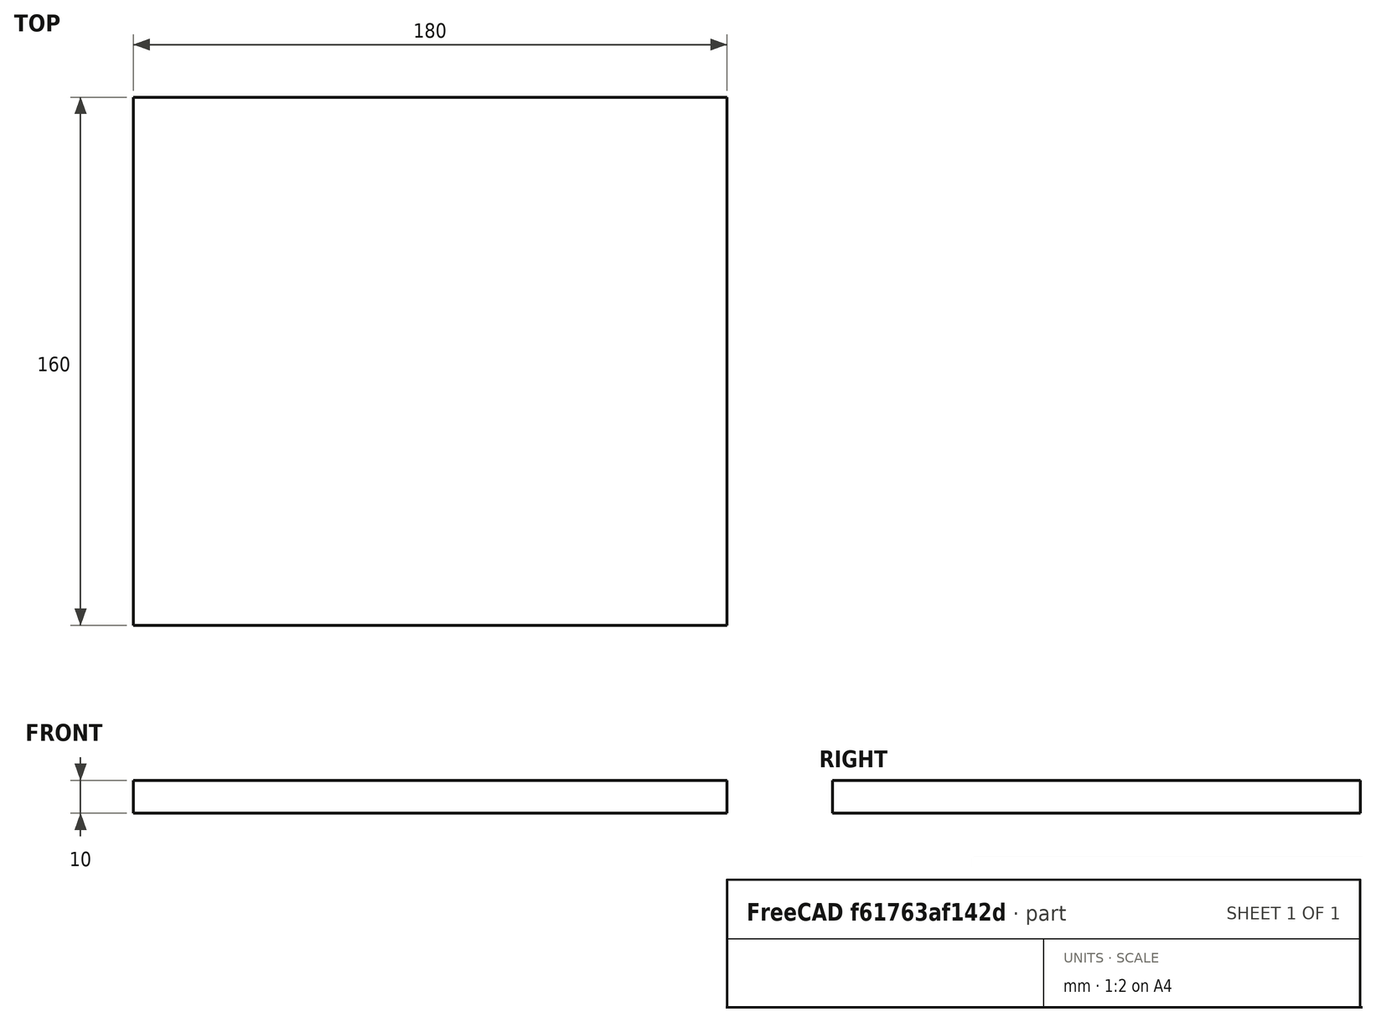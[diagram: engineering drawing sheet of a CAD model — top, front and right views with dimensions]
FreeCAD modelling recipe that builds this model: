
FCSTD DOCUMENT  (FreeCAD 0.18R4 (GitTag))
Label: BottomBaseMedium
License: All rights reserved
LicenseURL: http://en.wikipedia.org/wiki/All_rights_reserved
objects: Sketcher::SketchObject×1, PartDesign::Pad×1, PartDesign::Body×1
note: 4 computed .brp shape members not serialized (recipe doc carries the construction recipe); baked Part::Feature solids carry a one-line shape summary decoded from their .brp

FEATURE [Sketcher::SketchObject] Sketch
  MapMode = 5
  Support = -> [XY_Plane]
  sketch-geometry (4):
    g0: LineSegment StartX=0 StartY=0 StartZ=0 EndX=-180 EndY=0 EndZ=0
    g1: LineSegment StartX=-180 StartY=0 StartZ=0 EndX=-180 EndY=160 EndZ=0
    g2: LineSegment StartX=-180 StartY=160 StartZ=0 EndX=0 EndY=160 EndZ=0
    g3: LineSegment StartX=0 StartY=160 StartZ=0 EndX=0 EndY=0 EndZ=0
  constraints (11):
    c: Coincident(g0,g1)
    c: Coincident(g1,g2)
    c: Coincident(g2,g3)
    c: Coincident(g3,g0)
    c: Horizontal(g0)
    c: Horizontal(g2)
    c: Vertical(g1)
    c: Vertical(g3)
    c: Distance(g2) = 180
    c: Distance(g3) = 160
    c: Coincident(g0,g-1)
FEATURE [PartDesign::Pad] Pad
  Length = 10
  Length2 = 100
  Profile = -> Sketch
  Type = 0
FEATURE [PartDesign::Body] Body
  Group = -> [Sketch,Pad]
  Origin = -> Origin
  Tip = -> Pad
